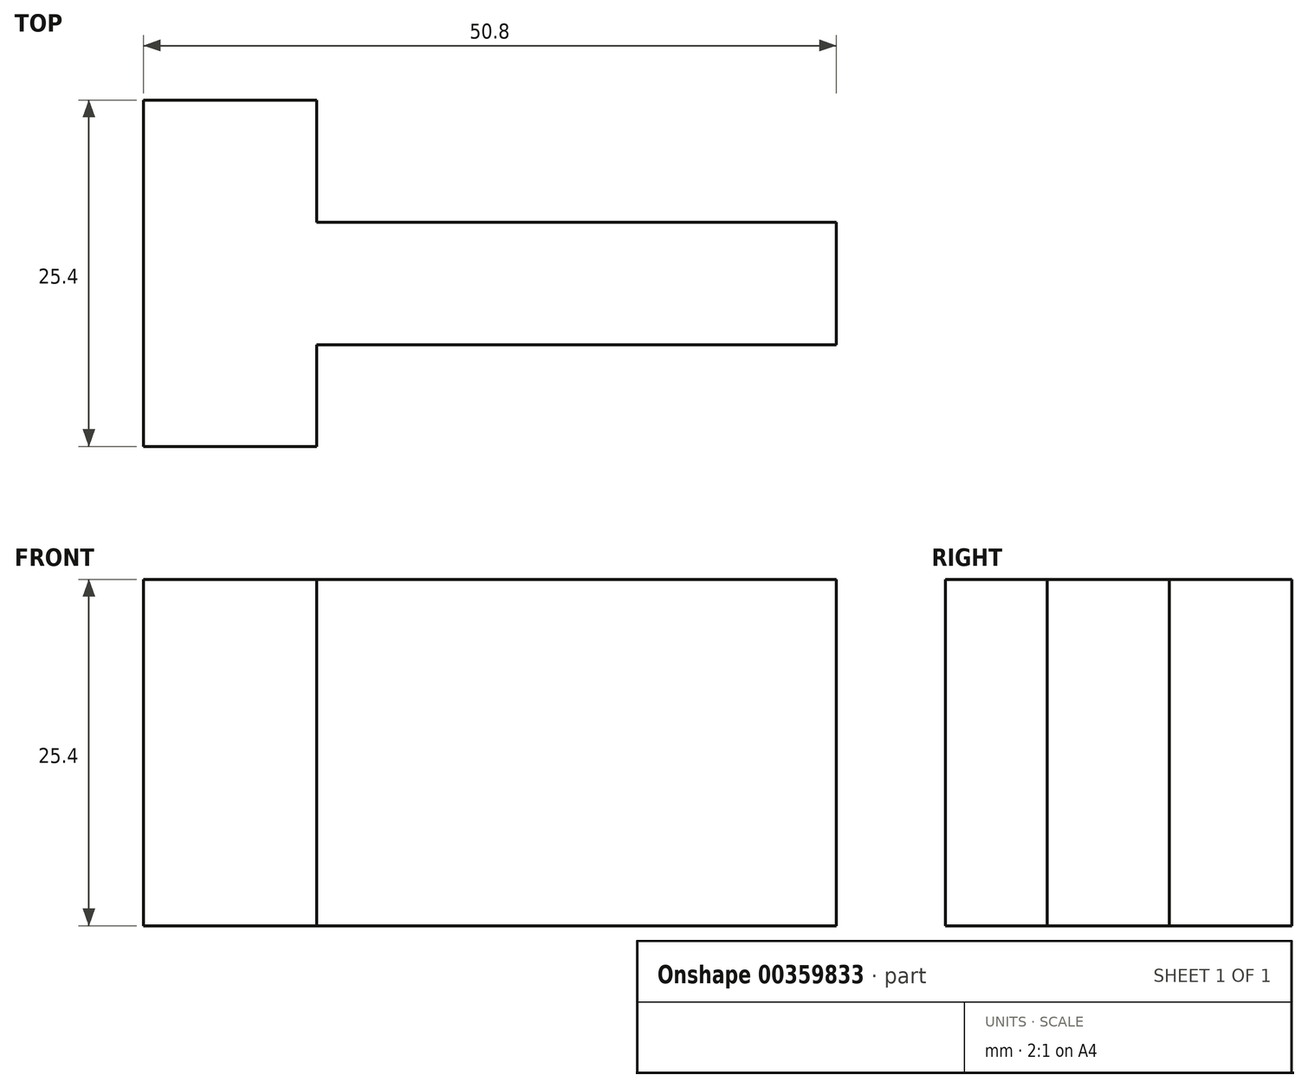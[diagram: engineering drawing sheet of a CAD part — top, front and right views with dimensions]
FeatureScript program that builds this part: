
annotation { "Feature Type Name" : "Feature", "Feature Type Description" : "" }
export const myFeature = defineFeature(function(context is Context, id is Id, definition is map)
    precondition{}
    {
        {
            var Q0;
            Q0=qCreatedBy(makeId("Top.planeOp"),FACE);
            var sketch = newSketch(context, id + "F0", { "sketchPlane" : qUnion([Q0])});
            skLineSegment(sketch, "E0", {"start": v(0, 0) * mm, "end": v(12.7, 0) * mm});
            skLineSegment(sketch, "E1", {"start": v(12.7, 0) * mm, "end": v(12.7, 7.45) * mm});
            skLineSegment(sketch, "E2", {"start": v(12.7, 7.45) * mm, "end": v(50.8, 7.45) * mm});
            skLineSegment(sketch, "E3", {"start": v(50.8, 7.45) * mm, "end": v(50.8, 16.42) * mm});
            skLineSegment(sketch, "E4", {"start": v(50.8, 16.42) * mm, "end": v(12.7, 16.42) * mm});
            skLineSegment(sketch, "E5", {"start": v(12.7, 16.42) * mm, "end": v(12.7, 25.4) * mm});
            skLineSegment(sketch, "E6", {"start": v(12.7, 25.4) * mm, "end": v(0, 25.4) * mm});
            skLineSegment(sketch, "E7", {"start": v(0, 0) * mm, "end": v(0, 25.4) * mm});
            skSolve(sketch);
        }
        {
            var Q0;
            Q0 = qSketchRegion(id + "F0", true);
            extrude(context, id + "F1", {"entities" : qUnion([Q0]), "depth" : 25.4 * mm});
        }
    });
